AUTODESK INVENTOR PART (.ipt)
format: ipt  version: 2021 (Build 250183000, 183)  size: 93,184 bytes
history: native  units: mm
features: extrude x1, sketch x1
ambient origin geometry x8: Origin, YZ Plane, XZ Plane, XY Plane, X Axis, Y Axis, Z Axis, Center Point
bodies: Solid1 (feature_tree)
feature tree (2):
  extrude  "Extrusion1"  Depth=8.2mm
  sketch  "Sketch1"  dims[d0=40.0mm d1=8.2mm d2=4.1mm d3=3.5mm d4=4.1mm d5=4.1mm d6=4.1mm d7=4.1mm d8=4.1mm d9=4.0mm d10=0.0mm]
